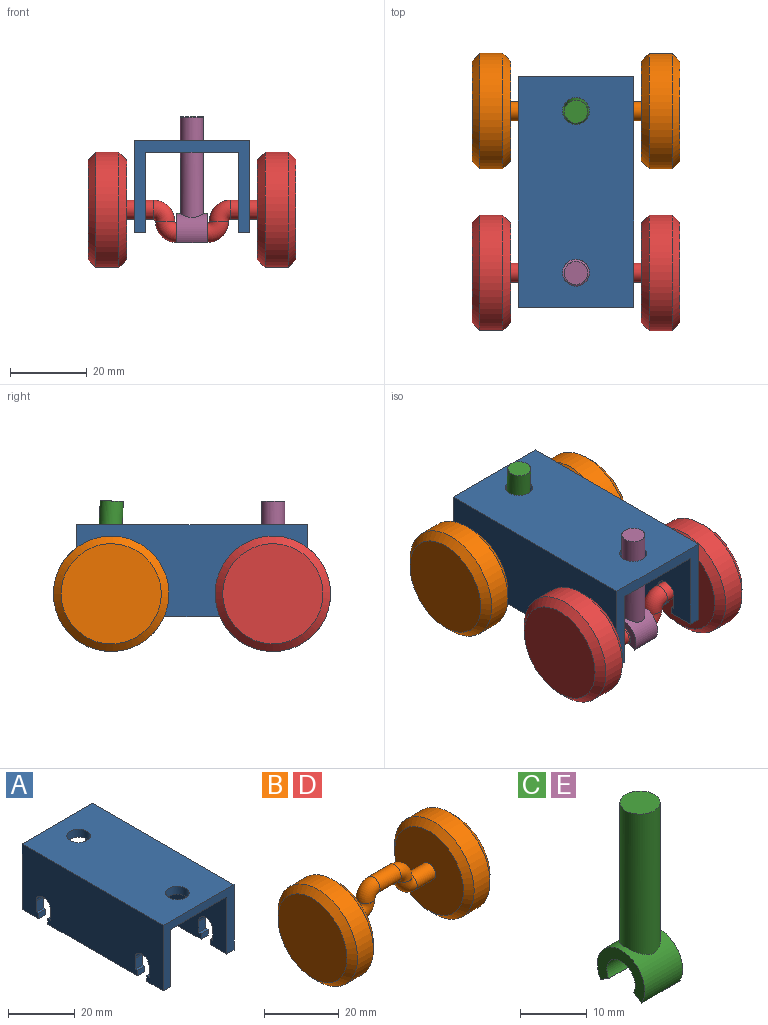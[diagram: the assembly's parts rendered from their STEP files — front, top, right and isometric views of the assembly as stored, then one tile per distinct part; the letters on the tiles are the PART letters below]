
ASSEMBLY  parts=5 mates=4
PART A: 44 faces, bbox 30x60x24 mm
  f0: plane 4x3mm, normal (0,1,0), area 12mm2, adj f8,f10,f17,f24
  f1: plane 4x3mm, normal (0,-1,0), area 12mm2, adj f8,f10,f17,f22
  f2: plane 38x3mm, normal (0,0,-1), area 114mm2, adj f4,f6,f19,f37
  f3: plane 38x3mm, normal (0,0,-1), area 114mm2, adj f8,f10,f23,f41
  f4: plane 60x24mm, normal (-1,0,0), area 1347.7mm2, adj f2,f5,f11,f12,f13,f14,f16,f18
  f5: plane 7x3mm, normal (0,0,-1), area 21mm2, adj f4,f6,f12,f21
  f6: plane 60x21mm, normal (1,0,0), area 1167.7mm2, adj f2,f5,f7,f12,f13,f14,f16,f18
  f7: plane 60x24mm, normal (0,0,-1), area 1363mm2, adj f6,f8,f12,f15,f30,f33
  f8: plane 60x21mm, normal (-1,0,0), area 1167.7mm2, adj f0,f1,f3,f7,f9,f12,f17,f22
  f9: plane 7x3mm, normal (0,0,-1), area 21mm2, adj f8,f10,f12,f25
  f10: plane 60x24mm, normal (1,0,0), area 1347.7mm2, adj f0,f1,f3,f9,f11,f12,f17,f22
  f11: plane 60x30mm, normal (0,0,1), area 1723mm2, adj f4,f10,f12,f15,f30,f33
  f12: plane 30x24mm, normal (0,-1,0), area 216mm2, adj f4,f5,f6,f7,f8,f9,f10,f11
  f13: plane 4x3mm, normal (0,1,0), area 12mm2, adj f4,f6,f16,f20
  f14: plane 4x3mm, normal (0,-1,0), area 12mm2, adj f4,f6,f16,f18
  f15: cylinder r=3.5mm len=7mm, axis (0,0,-1), area 66mm2, adj f7,f11
  f16: cylinder r=3mm len=6mm, axis (1,0,0), area 28.3mm2, adj f4,f6,f13,f14
  f17: cylinder r=3mm len=6mm, axis (1,0,0), area 28.3mm2, adj f0,f1,f8,f10
  f18: plane 3x1mm, normal (0,0,1), area 3mm2, adj f4,f6,f14,f19
  f19: plane 3x2mm, normal (0,-1,0), area 6mm2, adj f2,f4,f6,f18
  f20: plane 3x1mm, normal (0,0,1), area 3mm2, adj f4,f6,f13,f21
  f21: plane 3x2mm, normal (0,1,0), area 6mm2, adj f4,f5,f6,f20
  f22: plane 3x1mm, normal (0,0,1), area 3mm2, adj f1,f8,f10,f23
  f23: plane 3x2mm, normal (0,-1,0), area 6mm2, adj f3,f8,f10,f22
  f24: plane 3x1mm, normal (0,0,1), area 3mm2, adj f0,f8,f10,f25
  f25: plane 3x2mm, normal (0,1,0), area 6mm2, adj f8,f9,f10,f24
  f26: plane 4x3mm, normal (0,-1,0), area 12mm2, adj f8,f10,f35,f42
  f27: plane 4x3mm, normal (0,1,0), area 12mm2, adj f8,f10,f35,f40
  f28: plane 7x3mm, normal (0,0,-1), area 21mm2, adj f4,f6,f30,f39
  f29: plane 7x3mm, normal (0,0,-1), area 21mm2, adj f8,f10,f30,f43
  f30: plane 30x24mm, normal (0,1,0), area 216mm2, adj f4,f6,f7,f8,f10,f11,f28,f29
  f31: plane 4x3mm, normal (0,-1,0), area 12mm2, adj f4,f6,f34,f38
  f32: plane 4x3mm, normal (0,1,0), area 12mm2, adj f4,f6,f34,f36
  f33: cylinder r=3.5mm len=7mm, axis (0,0,-1), area 66mm2, adj f7,f11
  f34: cylinder r=3mm len=6mm, axis (1,0,0), area 28.3mm2, adj f4,f6,f31,f32
  f35: cylinder r=3mm len=6mm, axis (1,0,0), area 28.3mm2, adj f8,f10,f26,f27
  f36: plane 3x1mm, normal (0,0,1), area 3mm2, adj f4,f6,f32,f37
  f37: plane 3x2mm, normal (0,1,0), area 6mm2, adj f2,f4,f6,f36
  f38: plane 3x1mm, normal (0,0,1), area 3mm2, adj f4,f6,f31,f39
  f39: plane 3x2mm, normal (0,-1,0), area 6mm2, adj f4,f6,f28,f38
  f40: plane 3x1mm, normal (0,0,1), area 3mm2, adj f8,f10,f27,f41
  f41: plane 3x2mm, normal (0,1,0), area 6mm2, adj f3,f8,f10,f40
  f42: plane 3x1mm, normal (0,0,1), area 3mm2, adj f8,f10,f26,f43
  f43: plane 3x2mm, normal (0,-1,0), area 6mm2, adj f8,f10,f29,f42
PART B: 17 faces, bbox 54x30x30 mm
  f0: cylinder r=2.5mm len=7mm, axis (-1,0,0), area 110mm2, adj f1,f9
  f1: torus R=3mm, axis (0,1,0), area 74mm2, adj f0,f2
  f2: torus R=3mm, axis (0,-1,0), area 74mm2, adj f1,f3
  f3: cylinder r=2.5mm len=8mm, axis (-1,0,0), area 125.7mm2, adj f2,f4
  f4: torus R=3mm, axis (0,-1,0), area 74mm2, adj f3,f5
  f5: torus R=3mm, axis (0,1,0), area 74mm2, adj f4,f6
  f6: cylinder r=2.5mm len=7mm, axis (-1,0,0), area 110mm2, adj f5,f14
  f7: cylinder r=15mm len=30mm, axis (-1,0,0), area 565.5mm2, adj f10,f11
  f8: plane 26x26mm, normal (1,0,0), area 530.9mm2, adj f10
  f9: plane 26x26mm, normal (-1,0,0), area 511.3mm2, adj f0,f11
  f10: cone r=13mm half-angle=45deg, axis (-1,0,0), area 248.8mm2, adj f7,f8
  f11: cone r=15mm half-angle=45deg, axis (1,0,0), area 248.8mm2, adj f7,f9
  f12: cylinder r=15mm len=30mm, axis (1,0,0), area 565.5mm2, adj f15,f16
  f13: plane 26x26mm, normal (-1,0,0), area 530.9mm2, adj f15
  f14: plane 26x26mm, normal (1,0,0), area 511.3mm2, adj f6,f16
  f15: cone r=15mm half-angle=45deg, axis (1,0,0), area 248.8mm2, adj f12,f13
  f16: cone r=13mm half-angle=45deg, axis (-1,0,0), area 248.8mm2, adj f12,f14
PART C: 8 faces, bbox 8x10x32.5 mm
  f0: cylinder r=3mm len=8mm, axis (-1,0,0), area 100.5mm2, adj f1,f3,f4,f5
  f1: plane 8x1.73mm, normal (0,-0.5,-0.87), area 16mm2, adj f0,f2,f4,f5
  f2: cylinder r=5mm len=10mm, axis (-1,0,0), area 137.8mm2, adj f1,f3,f4,f5,f7
  f3: plane 8x1.73mm, normal (0,0.5,-0.87), area 16mm2, adj f0,f2,f4,f5
  f4: plane 10x7.5mm, normal (1,0,0), area 33.5mm2, adj f0,f1,f2,f3
  f5: plane 10x7.5mm, normal (-1,0,0), area 33.5mm2, adj f0,f1,f2,f3
  f6: plane 6x6mm, normal (0,0,1), area 28.3mm2, adj f7
  f7: cylinder r=3mm len=26mm, axis (0,0,1), area 480.4mm2, adj f2,f6
PART D: same geometry as B
PART E: same geometry as C
PLACE A t=(0,6,0)mm fixed
PLACE B rot(axis=(-1,0,0),167.9deg) t=(0,27,6)mm
PLACE C rot(axis=(1,0,0),2.7deg) t=(0,28.26,0.13)mm
PLACE D rot(axis=(1,0,0),179.7deg) t=(0,-15,6)mm
PLACE E rot(axis=(1,0,0),0.1deg) t=(0,-15.03,0)mm
MATE revolute C.f0 <-> B.f3  axis (-1,0,0) through (0,28.26,0.13)mm
MATE revolute E.f0 <-> D.f3  axis (-1,0,0) through (0,-15.03,0)mm
MATE revolute B.f0 <-> A.f34  axis (1,0,0) through (0,27,6)mm
MATE revolute A.f16 <-> D.f0  axis (1,0,0) through (0,-15,6)mm
